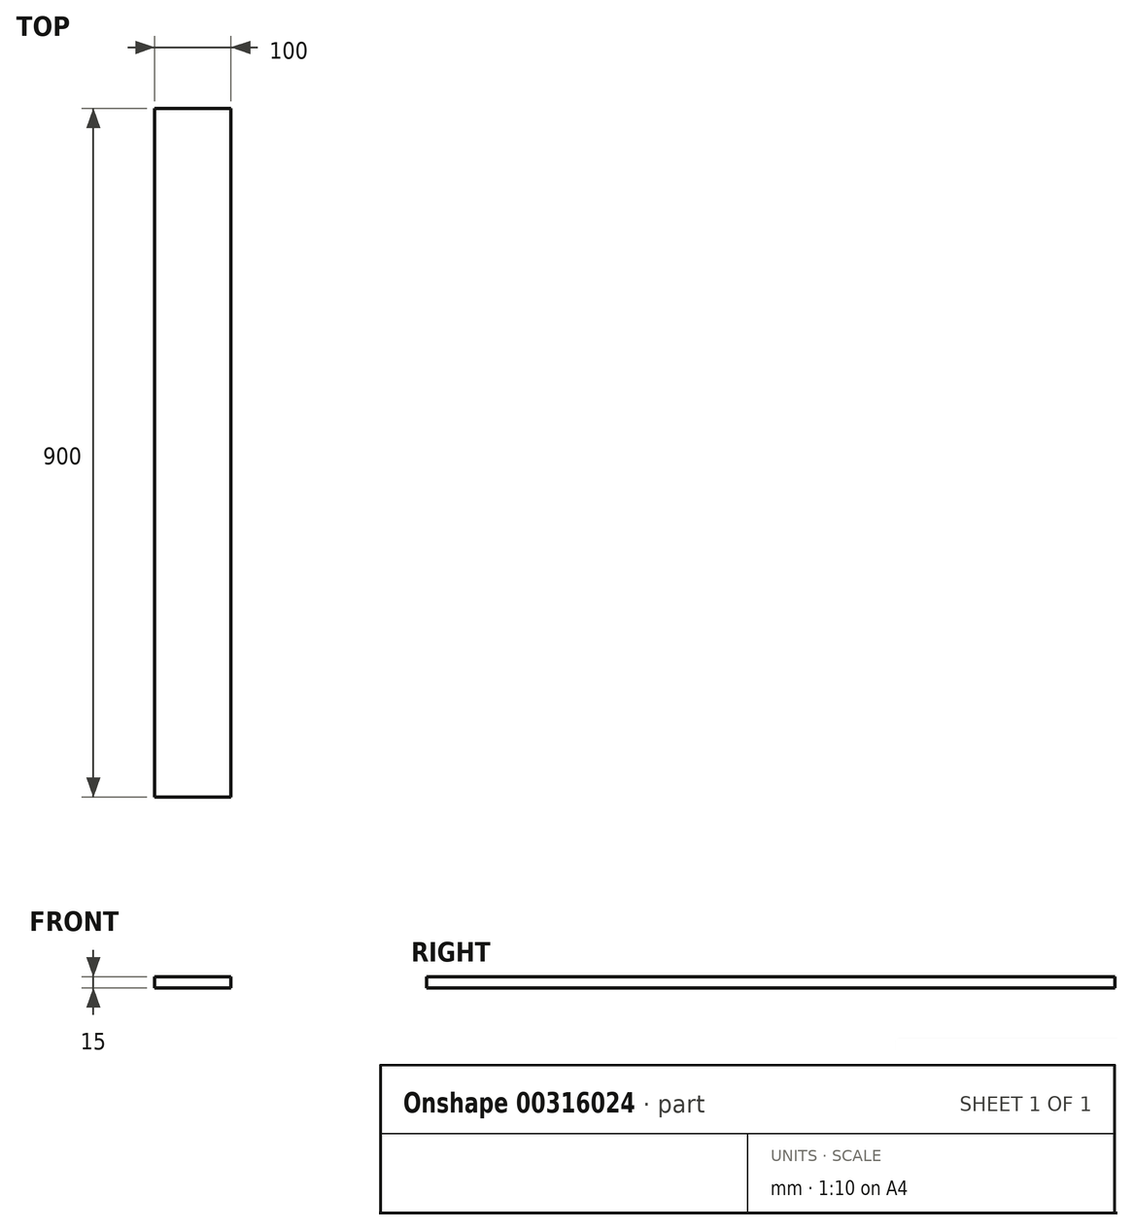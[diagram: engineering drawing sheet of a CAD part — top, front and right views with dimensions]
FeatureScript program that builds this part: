
annotation { "Feature Type Name" : "Feature", "Feature Type Description" : "" }
export const myFeature = defineFeature(function(context is Context, id is Id, definition is map)
    precondition{}
    {
        {
            var Q0;
            Q0=qCreatedBy(makeId("Front.planeOp"),FACE);
            var sketch = newSketch(context, id + "F0", { "sketchPlane" : qUnion([Q0])});
            skLineSegment(sketch, "E0.bottom", {"start": v(0, 0) * mm, "end": v(100, 0) * mm});
            skLineSegment(sketch, "E0.top", {"start": v(0, 15) * mm, "end": v(100, 15) * mm});
            skLineSegment(sketch, "E0.left", {"start": v(0, 0) * mm, "end": v(0, 15) * mm});
            skLineSegment(sketch, "E0.right", {"start": v(100, 0) * mm, "end": v(100, 15) * mm});
            skSolve(sketch);
        }
        {
            var Q0;
            Q0=qSketchRegion(id+"F0",true);
            extrude(context, id + "F1", {"entities" : qUnion([Q0]), "depth" : 900 * mm});
        }
    });
